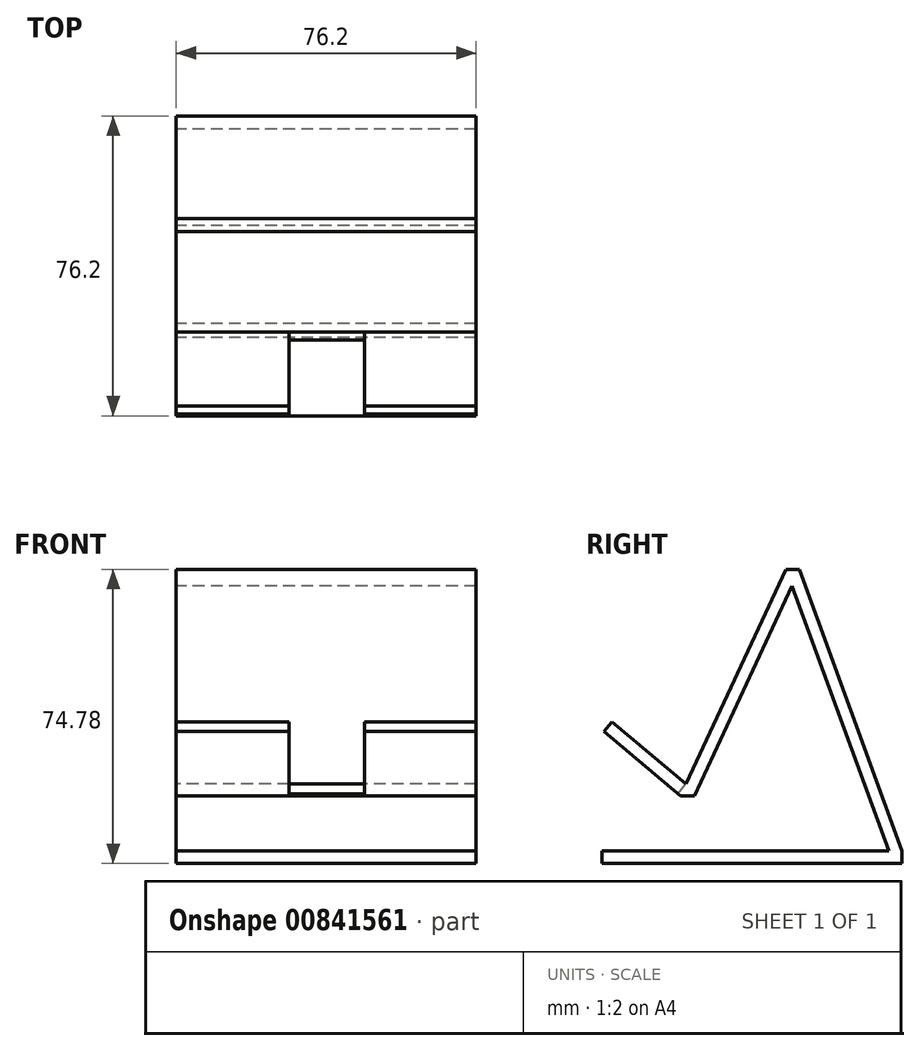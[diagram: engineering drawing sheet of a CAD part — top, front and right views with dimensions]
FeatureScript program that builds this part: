
annotation { "Feature Type Name" : "Feature", "Feature Type Description" : "" }
export const myFeature = defineFeature(function(context is Context, id is Id, definition is map)
    precondition{}
    {
        {
            var Q0;
            Q0=qCreatedBy(makeId("Top.planeOp"),FACE);
            var sketch = newSketch(context, id + "F0", { "sketchPlane" : qUnion([Q0])});
            skLineSegment(sketch, "E0.bottom", {"start": v(-50.93, 28.39) * mm, "end": v(25.27, 28.39) * mm});
            skLineSegment(sketch, "E0.top", {"start": v(-50.93, -47.81) * mm, "end": v(25.27, -47.81) * mm});
            skLineSegment(sketch, "E0.left", {"start": v(-50.93, 28.39) * mm, "end": v(-50.93, -47.81) * mm});
            skLineSegment(sketch, "E0.right", {"start": v(25.27, 28.39) * mm, "end": v(25.27, -47.81) * mm});
            skSolve(sketch);
        }
        {
            var Q0;
            Q0=qSketchRegion(id+"F0",true);
            extrude(context, id + "F1", {"entities" : qUnion([Q0]), "depth" : 3.17 * mm, "offsetDistance" : 25.4 * mm});
        }
        {
            var Q0;
            Q0=makeQuery(id+"F1.opExtrude","SWEPT_FACE",FACE,{"disambiguationData":[OSD([sQuery(id+"F0.wireOp",EDGE,"E0.left")])]});
            var sketch = newSketch(context, id + "F2", { "sketchPlane" : qUnion([Q0])});
            skLineSegment(sketch, "E1", {"start": v(-28.39, 3.17) * mm, "end": v(-2.33, 74.78) * mm});
            skLineSegment(sketch, "E2", {"start": v(-25, 3.18) * mm, "end": v(1.05, 74.78) * mm});
            skLineSegment(sketch, "E3", {"start": v(1.05, 74.78) * mm, "end": v(-2.33, 74.78) * mm});
            skLineSegment(sketch, "E4", {"start": v(27.89, 17.23) * mm, "end": v(1.05, 74.78) * mm});
            skLineSegment(sketch, "E5", {"start": v(47.35, 33.56) * mm, "end": v(27.89, 17.23) * mm});
            skLineSegment(sketch, "E6", {"start": v(-0.48, 70.56) * mm, "end": v(24.39, 17.23) * mm});
            skLineSegment(sketch, "E7", {"start": v(24.39, 17.23) * mm, "end": v(27.89, 17.23) * mm});
            skLineSegment(sketch, "E8", {"start": v(47.35, 33.56) * mm, "end": v(45.3, 35.99) * mm});
            skLineSegment(sketch, "E9", {"start": v(45.3, 35.99) * mm, "end": v(26.5, 20.2) * mm});
            skSolve(sketch);
        }
        {
            var Q0;
            Q0=qSketchRegion(id+"F2",true);
            var Q1;
            {var subQ6=sQuery(id+"F2.wireOp",EDGE,"E1");Q1=makeQuery(id+"F2.imprint","IMPRINT",FACE,{"disambiguationData":[TD([[makeQuery(id+"F2.imprint","IMPRINT",EDGE,{"derivedFrom":subQ6}),-1.0]])]});}
            extrude(context, id + "F3", {"entities" : qUnion([Q0, Q1]), "operationType" : NewBodyOperationType.ADD, "oppositeDirection" : true, "depth" : 76.2 * mm, "offsetDistance" : 25.4 * mm});
        }
        {
            var Q0;
            Q0=makeQuery(id+"F3.opExtrude","SWEPT_FACE",FACE,{"disambiguationData":[OSD([sQuery(id+"F2.wireOp",EDGE,"E9")])]});
            var sketch = newSketch(context, id + "F4", { "sketchPlane" : qUnion([Q0])});
            skLineSegment(sketch, "E10.bottom", {"start": v(-22.25, -33.29) * mm, "end": v(-3.15, -33.29) * mm});
            skLineSegment(sketch, "E10.top", {"start": v(-22.25, -65.96) * mm, "end": v(-3.15, -65.96) * mm});
            skLineSegment(sketch, "E10.left", {"start": v(-22.25, -33.29) * mm, "end": v(-22.25, -65.96) * mm});
            skLineSegment(sketch, "E10.right", {"start": v(-3.15, -33.29) * mm, "end": v(-3.15, -65.96) * mm});
            skSolve(sketch);
        }
        {
            var Q0;
            {var subQ0=sQuery(id+"F4.wireOp",EDGE,"E10.bottom");Q0=makeQuery(id+"F4.imprint","IMPRINT",FACE,{"disambiguationData":[TD([[makeQuery(id+"F4.imprint","IMPRINT",EDGE,{"derivedFrom":subQ0}),1.0]])]});}
            extrude(context, id + "F5", {"entities" : qUnion([Q0]), "operationType" : NewBodyOperationType.REMOVE, "oppositeDirection" : true, "depth" : 4 * mm, "offsetDistance" : 25 * mm});
        }
    });
